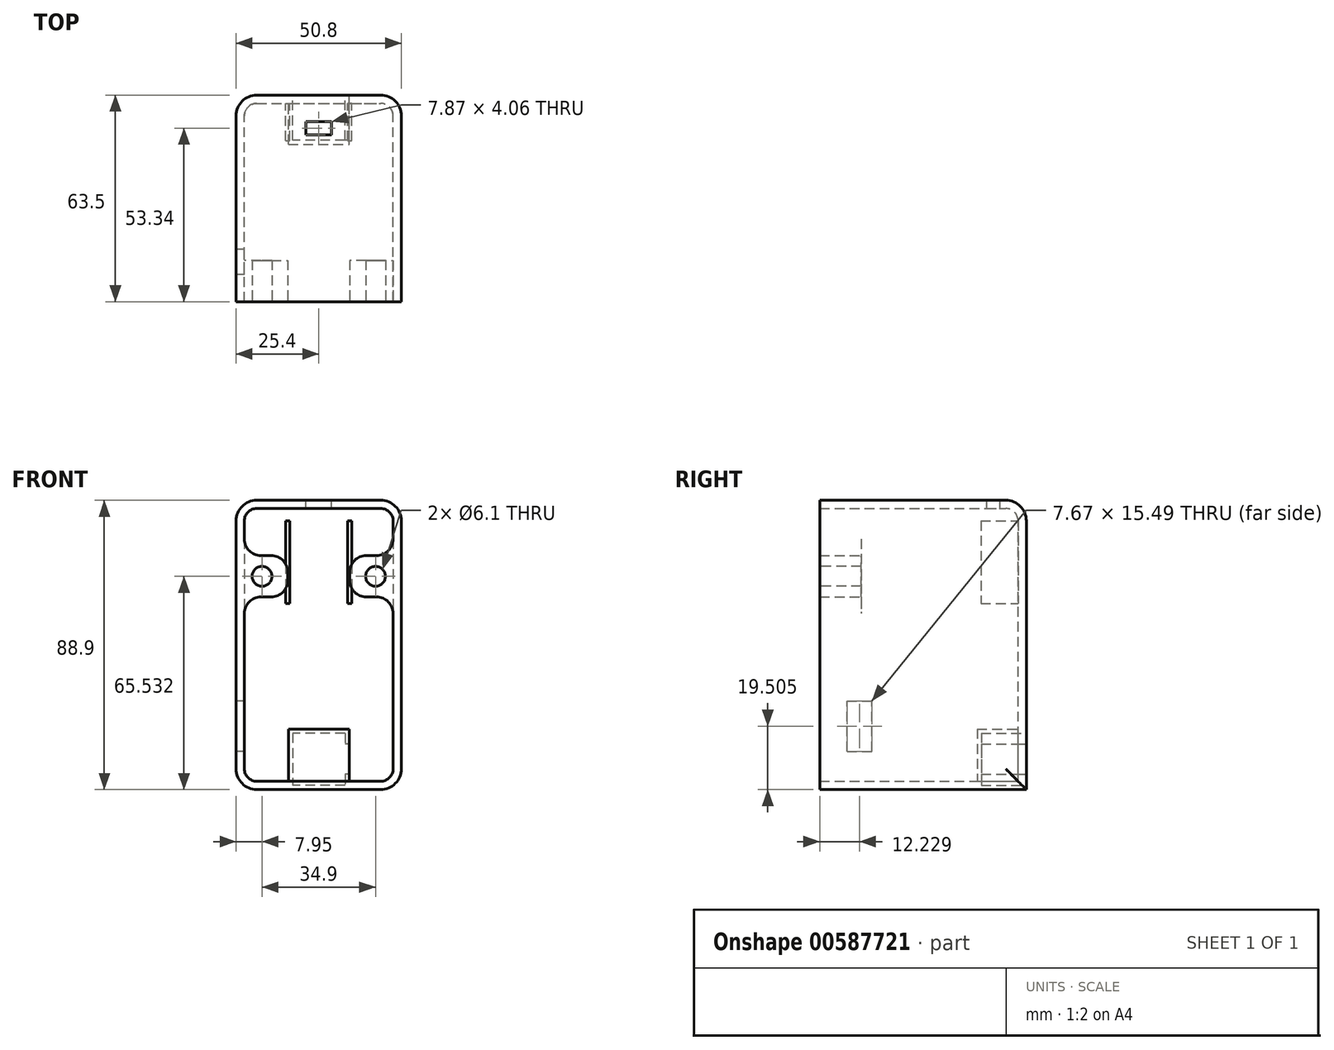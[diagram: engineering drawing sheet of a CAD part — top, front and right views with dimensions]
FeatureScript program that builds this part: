
annotation { "Feature Type Name" : "Feature", "Feature Type Description" : "" }
export const myFeature = defineFeature(function(context is Context, id is Id, definition is map)
    precondition{}
    {
        {
            var Q0;
            Q0=qCreatedBy(makeId("Front.planeOp"),FACE);
            var sketch = newSketch(context, id + "F0", { "sketchPlane" : qUnion([Q0])});
            skLineSegment(sketch, "E0.bottom", {"start": v(-25.4, 44.45) * mm, "end": v(25.4, 44.45) * mm});
            skLineSegment(sketch, "E0.top", {"start": v(-25.4, -44.45) * mm, "end": v(25.4, -44.45) * mm});
            skLineSegment(sketch, "E0.left", {"start": v(-25.4, 44.45) * mm, "end": v(-25.4, -44.45) * mm});
            skLineSegment(sketch, "E0.right", {"start": v(25.4, 44.45) * mm, "end": v(25.4, -44.45) * mm});
            skPoint(sketch, "E0.middle", {"position": v(0, 0) * mm});
            skSolve(sketch);
        }
        {
            var Q0;
            Q0 = qSketchRegion(id + "F0", true);
            extrude(context, id + "F1", {"entities" : qUnion([Q0]), "depth" : 63.5 * mm, "offsetDistance" : 25.4 * mm});
        }
        {
            var Q0;
            Q0=makeQuery(id+"F1.opExtrude","SWEPT_EDGE",EDGE,{"disambiguationData":[OSD([sQuery(id+"F0.wireOp",EDGE,"E0.bottom"),sQuery(id+"F0.wireOp",EDGE,"E0.right")])]});
            var Q1;
            Q1=makeQuery(id+"F1.opExtrude","SWEPT_EDGE",EDGE,{"disambiguationData":[OSD([sQuery(id+"F0.wireOp",EDGE,"E0.bottom"),sQuery(id+"F0.wireOp",EDGE,"E0.left")])]});
            var Q2;
            Q2=makeQuery(id+"F1.opExtrude","CAP_EDGE",EDGE,{"disambiguationData":[OSD([sQuery(id+"F0.wireOp",EDGE,"E0.bottom")])],"isStart":true});
            var Q3;
            Q3=makeQuery(id+"F1.opExtrude","SWEPT_EDGE",EDGE,{"disambiguationData":[OSD([sQuery(id+"F0.wireOp",EDGE,"E0.top"),sQuery(id+"F0.wireOp",EDGE,"E0.right")])]});
            var Q4;
            Q4=makeQuery(id+"F1.opExtrude","SWEPT_EDGE",EDGE,{"disambiguationData":[OSD([sQuery(id+"F0.wireOp",EDGE,"E0.top"),sQuery(id+"F0.wireOp",EDGE,"E0.left")])]});
            var Q5;
            Q5=makeQuery(id+"F1.opExtrude","CAP_EDGE",EDGE,{"disambiguationData":[OSD([sQuery(id+"F0.wireOp",EDGE,"E0.right")])],"isStart":true});
            var Q6;
            Q6=makeQuery(id+"F1.opExtrude","CAP_EDGE",EDGE,{"disambiguationData":[OSD([sQuery(id+"F0.wireOp",EDGE,"E0.left")])],"isStart":true});
            fillet(context, id + "F2", {"entities" : qUnion([Q0, Q1, Q2, Q3, Q4, Q5, Q6]), "radius" : 6.35 * mm, "tangentPropagation" : true, "allowEdgeOverflow" : false});
        }
        {
            var Q0;
            Q0=makeQuery(id+"F1.opExtrude","CAP_FACE",FACE,{"disambiguationData":[OSD([sQuery(id+"F0.wireOp",EDGE,"E0.bottom"),sQuery(id+"F0.wireOp",EDGE,"E0.top"),sQuery(id+"F0.wireOp",EDGE,"E0.left"),sQuery(id+"F0.wireOp",EDGE,"E0.right")])],"isStart":false});
            shell(context, id + "F3", {"entities" : qUnion([Q0]), "thickness" : 2.54 * mm});
        }
        {
            var Q0;
            Q0=makeQuery(id+"F1.opExtrude","CAP_FACE",FACE,{"disambiguationData":[OSD([sQuery(id+"F0.wireOp",EDGE,"E0.bottom"),sQuery(id+"F0.wireOp",EDGE,"E0.top"),sQuery(id+"F0.wireOp",EDGE,"E0.left"),sQuery(id+"F0.wireOp",EDGE,"E0.right")])],"isStart":false});
            var sketch = newSketch(context, id + "F4", { "sketchPlane" : qUnion([Q0])});
            skLineSegment(sketch, "E1.bottom", {"start": v(-25.4, 27.43) * mm, "end": v(-9.5, 27.43) * mm});
            skLineSegment(sketch, "E1.top", {"start": v(-25.4, 14.73) * mm, "end": v(-9.5, 14.73) * mm});
            skLineSegment(sketch, "E1.left", {"start": v(-25.4, 27.43) * mm, "end": v(-25.4, 14.73) * mm});
            skLineSegment(sketch, "E1.right", {"start": v(-9.5, 27.43) * mm, "end": v(-9.5, 14.73) * mm});
            skCircle(sketch, "E2", {"center": v(-17.45, 21.08) * mm, "radius": 3.05 * mm});
            skPoint(sketch, "E2.centerSnap0", {"position": v(-9.5, 21.08) * mm});
            skPoint(sketch, "E2.centerSnap1", {"position": v(-17.45, 27.43) * mm});
            skLineSegment(sketch, "E3", {"start": v(0, 84.41) * mm, "end": v(0, -83.5) * mm, "construction": true});
            skLineSegment(sketch, "E4.MirrorCS", {"start": v(25.4, 27.43) * mm, "end": v(9.5, 27.43) * mm});
            skLineSegment(sketch, "E5.MirrorCS", {"start": v(9.5, 27.43) * mm, "end": v(9.5, 14.73) * mm});
            skLineSegment(sketch, "E6.MirrorCS", {"start": v(25.4, 14.73) * mm, "end": v(9.5, 14.73) * mm});
            skCircle(sketch, "E7.MirrorC", {"center": v(17.45, 21.08) * mm, "radius": 3.05 * mm});
            skLineSegment(sketch, "E8", {"start": v(25.4, 27.43) * mm, "end": v(25.4, 14.73) * mm});
            skSolve(sketch);
        }
        {
            var Q0;
            Q0 = qSketchRegion(id + "F4", true);
            extrude(context, id + "F5", {"entities" : qUnion([Q0]), "operationType" : NewBodyOperationType.ADD, "oppositeDirection" : true, "depth" : 12.7 * mm, "offsetDistance" : 25.4 * mm});
        }
        {
            var Q0;
            Q0=makeQuery(id+"F5.opExtrude","SWEPT_EDGE",EDGE,{"disambiguationData":[OSD([sQuery(id+"F4.wireOp",EDGE,"E1.bottom"),sQuery(id+"F4.wireOp",EDGE,"E1.right")])]});
            var Q1;
            Q1=makeQuery(id+"F5.opExtrude","SWEPT_EDGE",EDGE,{"disambiguationData":[OSD([sQuery(id+"F4.wireOp",EDGE,"E1.top"),sQuery(id+"F4.wireOp",EDGE,"E1.right")])]});
            var Q2;
            Q2=makeQuery(id+"F5.opExtrude","SWEPT_EDGE",EDGE,{"disambiguationData":[OSD([sQuery(id+"F4.wireOp",EDGE,"E5.MirrorCS"),sQuery(id+"F4.wireOp",EDGE,"E6.MirrorCS")])]});
            var Q3;
            Q3=makeQuery(id+"F5.opExtrude","SWEPT_EDGE",EDGE,{"disambiguationData":[OSD([sQuery(id+"F4.wireOp",EDGE,"E4.MirrorCS"),sQuery(id+"F4.wireOp",EDGE,"E5.MirrorCS")])]});
            var Q4;
            {var subQ0=sQuery(id+"F0.wireOp",EDGE,"E0.left");Q4=makeQuery(id+"F5.boolean.opBoolean","INTERSECT",EDGE,{"derivedFrom":[makeQuery(id+"F3.opShell","OFFSET_FACE",FACE,{"disambiguationData":[OSD([subQ0]),TDD([makeQuery(id+"F1.opExtrude","SWEPT_FACE",FACE,{"disambiguationData":[OSD([subQ0])]})])]}),makeQuery(id+"F5.opExtrude","SWEPT_FACE",FACE,{"disambiguationData":[OSD([sQuery(id+"F4.wireOp",EDGE,"E1.bottom")])]})]});}
            var Q5;
            {var subQ0=sQuery(id+"F0.wireOp",EDGE,"E0.right");Q5=makeQuery(id+"F5.boolean.opBoolean","INTERSECT",EDGE,{"derivedFrom":[makeQuery(id+"F3.opShell","OFFSET_FACE",FACE,{"disambiguationData":[OSD([subQ0]),TDD([makeQuery(id+"F1.opExtrude","SWEPT_FACE",FACE,{"disambiguationData":[OSD([subQ0])]})])]}),makeQuery(id+"F5.opExtrude","SWEPT_FACE",FACE,{"disambiguationData":[OSD([sQuery(id+"F4.wireOp",EDGE,"E4.MirrorCS")])]})]});}
            var Q6;
            {var subQ0=sQuery(id+"F0.wireOp",EDGE,"E0.left");Q6=makeQuery(id+"F5.boolean.opBoolean","INTERSECT",EDGE,{"derivedFrom":[makeQuery(id+"F3.opShell","OFFSET_FACE",FACE,{"disambiguationData":[OSD([subQ0]),TDD([makeQuery(id+"F1.opExtrude","SWEPT_FACE",FACE,{"disambiguationData":[OSD([subQ0])]})])]}),makeQuery(id+"F5.opExtrude","SWEPT_FACE",FACE,{"disambiguationData":[OSD([sQuery(id+"F4.wireOp",EDGE,"E1.top")])]})]});}
            var Q7;
            {var subQ0=sQuery(id+"F0.wireOp",EDGE,"E0.right");Q7=makeQuery(id+"F5.boolean.opBoolean","INTERSECT",EDGE,{"derivedFrom":[makeQuery(id+"F3.opShell","OFFSET_FACE",FACE,{"disambiguationData":[OSD([subQ0]),TDD([makeQuery(id+"F1.opExtrude","SWEPT_FACE",FACE,{"disambiguationData":[OSD([subQ0])]})])]}),makeQuery(id+"F5.opExtrude","SWEPT_FACE",FACE,{"disambiguationData":[OSD([sQuery(id+"F4.wireOp",EDGE,"E6.MirrorCS")])]})]});}
            fillet(context, id + "F6", {"entities" : qUnion([Q0, Q1, Q2, Q3, Q4, Q5, Q6, Q7]), "radius" : 5.08 * mm, "tangentPropagation" : true, "allowEdgeOverflow" : false});
        }
        {
            var Q0;
            Q0=makeQuery(id+"F1.opExtrude","SWEPT_FACE",FACE,{"disambiguationData":[OSD([sQuery(id+"F0.wireOp",EDGE,"E0.bottom")])]});
            var sketch = newSketch(context, id + "F7", { "sketchPlane" : qUnion([Q0])});
            skLineSegment(sketch, "E9.bottom", {"start": v(3.94, -12.2) * mm, "end": v(-3.94, -12.2) * mm});
            skLineSegment(sketch, "E9.top", {"start": v(3.94, -8.13) * mm, "end": v(-3.94, -8.13) * mm});
            skLineSegment(sketch, "E9.left", {"start": v(3.94, -12.2) * mm, "end": v(3.94, -8.13) * mm});
            skLineSegment(sketch, "E9.right", {"start": v(-3.94, -12.2) * mm, "end": v(-3.94, -8.13) * mm});
            skPoint(sketch, "E9.middle", {"position": v(0, -10.16) * mm});
            skSolve(sketch);
        }
        {
            var Q0;
            Q0 = qSketchRegion(id + "F7", true);
            extrude(context, id + "F8", {"entities" : qUnion([Q0]), "operationType" : NewBodyOperationType.REMOVE, "oppositeDirection" : true, "depth" : 25.4 * mm, "offsetDistance" : 25.4 * mm});
        }
        {
            var Q0;
            Q0=makeQuery(id+"F3.opShell","OFFSET_FACE",FACE,{"disambiguationData":[OSD([sQuery(id+"F0.wireOp",EDGE,"E0.bottom"),sQuery(id+"F0.wireOp",EDGE,"E0.top"),sQuery(id+"F0.wireOp",EDGE,"E0.left"),sQuery(id+"F0.wireOp",EDGE,"E0.right")])]});
            var sketch = newSketch(context, id + "F9", { "sketchPlane" : qUnion([Q0])});
            skLineSegment(sketch, "E10.bottom", {"start": v(-10.16, 38.1) * mm, "end": v(-8.9, 38.1) * mm});
            skLineSegment(sketch, "E10.top", {"start": v(-10.16, 12.7) * mm, "end": v(-8.9, 12.7) * mm});
            skLineSegment(sketch, "E10.left", {"start": v(-10.16, 38.1) * mm, "end": v(-10.16, 12.7) * mm});
            skLineSegment(sketch, "E10.right", {"start": v(-8.9, 38.1) * mm, "end": v(-8.9, 12.7) * mm});
            skLineSegment(sketch, "E11", {"start": v(0, 0) * mm, "end": v(0, 27.98) * mm, "construction": true});
            skLineSegment(sketch, "E12.MirrorCS", {"start": v(10.16, 38.1) * mm, "end": v(8.9, 38.1) * mm});
            skLineSegment(sketch, "E13.MirrorCS", {"start": v(10.16, 12.7) * mm, "end": v(8.9, 12.7) * mm});
            skLineSegment(sketch, "E14.MirrorCS", {"start": v(10.16, 38.1) * mm, "end": v(10.16, 12.7) * mm});
            skLineSegment(sketch, "E15.MirrorCS", {"start": v(8.9, 38.1) * mm, "end": v(8.9, 12.7) * mm});
            skSolve(sketch);
        }
        {
            var Q0;
            Q0 = qSketchRegion(id + "F9", true);
            extrude(context, id + "F10", {"entities" : qUnion([Q0]), "operationType" : NewBodyOperationType.ADD, "depth" : 11.43 * mm, "offsetDistance" : 25.4 * mm});
        }
        {
            var Q0;
            Q0=makeQuery(id+"F1.opExtrude","CAP_FACE",FACE,{"disambiguationData":[OSD([sQuery(id+"F0.wireOp",EDGE,"E0.bottom"),sQuery(id+"F0.wireOp",EDGE,"E0.top"),sQuery(id+"F0.wireOp",EDGE,"E0.left"),sQuery(id+"F0.wireOp",EDGE,"E0.right")])],"isStart":true});
            var sketch = newSketch(context, id + "F11", { "sketchPlane" : qUnion([Q0])});
            skLineSegment(sketch, "E16.bottom", {"start": v(-8.06, -27.13) * mm, "end": v(8.06, -27.13) * mm});
            skLineSegment(sketch, "E16.top", {"start": v(-8.06, -43.18) * mm, "end": v(8.06, -43.18) * mm});
            skLineSegment(sketch, "E16.left", {"start": v(-8.06, -27.13) * mm, "end": v(-8.06, -43.18) * mm});
            skLineSegment(sketch, "E16.right", {"start": v(8.06, -27.13) * mm, "end": v(8.06, -43.18) * mm});
            skPoint(sketch, "E17", {"position": v(0, -27.13) * mm});
            skLineSegment(sketch, "E18.bottom", {"start": v(-9.33, -25.86) * mm, "end": v(9.33, -25.86) * mm});
            skLineSegment(sketch, "E18.top", {"start": v(-9.33, -44.45) * mm, "end": v(9.33, -44.45) * mm});
            skLineSegment(sketch, "E18.left", {"start": v(-9.33, -25.86) * mm, "end": v(-9.33, -44.45) * mm});
            skLineSegment(sketch, "E18.right", {"start": v(9.33, -25.86) * mm, "end": v(9.33, -44.45) * mm});
            skSolve(sketch);
        }
        {
            var Q0;
            {var subQ0=sQuery(id+"F11.wireOp",EDGE,"E16.bottom");Q0=makeQuery(id+"F11.imprint","IMPRINT",FACE,{"disambiguationData":[TD([[makeQuery(id+"F11.imprint","IMPRINT",EDGE,{"derivedFrom":subQ0}),-1.0]])]});}
            var Q1;
            {var subQ0=sQuery(id+"F11.wireOp",EDGE,"E16.top");Q1=makeQuery(id+"F11.imprint","IMPRINT",FACE,{"disambiguationData":[TD([[makeQuery(id+"F11.imprint","IMPRINT",EDGE,{"derivedFrom":subQ0}),1.0]])]});}
            extrude(context, id + "F12", {"entities" : qUnion([Q0, Q1]), "operationType" : NewBodyOperationType.REMOVE, "oppositeDirection" : true, "depth" : 13.84 * mm, "offsetDistance" : 25.4 * mm});
        }
        {
            var Q0;
            Q0=makeQuery(id+"F11.imprint","IMPRINT",FACE,{"disambiguationData":[TD([[makeQuery(id+"F11.imprint","IMPRINT",EDGE,{"derivedFrom":sQuery(id+"F11.wireOp",EDGE,"E16.bottom")}),1.0]])]});
            extrude(context, id + "F13", {"entities" : qUnion([Q0]), "operationType" : NewBodyOperationType.ADD, "oppositeDirection" : true, "depth" : 13.84 * mm, "offsetDistance" : 25.4 * mm});
        }
        {
            var Q0;
            Q0=makeQuery(id+"F11.imprint","IMPRINT",FACE,{"disambiguationData":[TD([[makeQuery(id+"F11.imprint","IMPRINT",EDGE,{"derivedFrom":sQuery(id+"F11.wireOp",EDGE,"E18.bottom")}),1.0]])]});
            var sketch = newSketch(context, id + "F14", { "sketchPlane" : qUnion([Q0])});
            skLineSegment(sketch, "E19.bottom", {"start": v(-9.33, -30.52) * mm, "end": v(-5.57, -30.52) * mm});
            skLineSegment(sketch, "E19.top", {"start": v(-9.33, -39.79) * mm, "end": v(-5.57, -39.79) * mm});
            skLineSegment(sketch, "E19.left", {"start": v(-9.33, -30.52) * mm, "end": v(-9.33, -39.79) * mm});
            skLineSegment(sketch, "E19.right", {"start": v(-5.57, -30.52) * mm, "end": v(-5.57, -39.79) * mm});
            skPoint(sketch, "E19.middle", {"position": v(-7.45, -35.15) * mm});
            skPoint(sketch, "E20", {"position": v(-9.33, -35.15) * mm});
            skSolve(sketch);
        }
        {
            var Q0;
            Q0 = qSketchRegion(id + "F14", true);
            extrude(context, id + "F15", {"entities" : qUnion([Q0]), "operationType" : NewBodyOperationType.REMOVE, "oppositeDirection" : true, "depth" : 13.84 * mm, "offsetDistance" : 25.4 * mm});
        }
        {
            var Q0;
            {var subQ0=sQuery(id+"F11.wireOp",EDGE,"E18.bottom");var subQ1=sQuery(id+"F11.wireOp",EDGE,"E16.left");var subQ2=sQuery(id+"F11.wireOp",EDGE,"E16.bottom");var subQ3=sQuery(id+"F11.wireOp",EDGE,"E16.right");var subQ4=sQuery(id+"F11.wireOp",EDGE,"E18.left");var subQ5=sQuery(id+"F11.wireOp",EDGE,"E16.top");var subQ6=sQuery(id+"F11.wireOp",EDGE,"E18.right");Q0=makeQuery(id+"F15.boolean.opBoolean","SPLIT",FACE,{"disambiguationData":[TD([makeQuery(id+"F12.boolean.opBoolean","COPY",FACE,{"derivedFrom":makeQuery(id+"F12.opExtrude","SWEPT_FACE",FACE,{"disambiguationData":[OSD([subQ2])]})})])],"derivedFrom":makeQuery(id+"F13.opExtrude","CAP_FACE",FACE,{"disambiguationData":[OSD([subQ2,subQ5,subQ1,subQ3,subQ0,sQuery(id+"F11.wireOp",EDGE,"E18.top"),subQ4,subQ6])],"isStart":false})});}
            var sketch = newSketch(context, id + "F16", { "sketchPlane" : qUnion([Q0])});
            skLineSegment(sketch, "E21.bottom", {"start": v(-9.33, -25.86) * mm, "end": v(9.33, -25.86) * mm});
            skLineSegment(sketch, "E21.top", {"start": v(-9.33, -44.45) * mm, "end": v(9.33, -44.45) * mm});
            skLineSegment(sketch, "E21.left", {"start": v(-9.33, -25.86) * mm, "end": v(-9.33, -44.45) * mm});
            skLineSegment(sketch, "E21.right", {"start": v(9.33, -25.86) * mm, "end": v(9.33, -44.45) * mm});
            skSolve(sketch);
        }
        {
            var Q0;
            Q0 = qSketchRegion(id + "F16", true);
            extrude(context, id + "F17", {"entities" : qUnion([Q0]), "operationType" : NewBodyOperationType.ADD, "depth" : 1.27 * mm, "offsetDistance" : 25.4 * mm});
        }
        {
            var Q0;
            Q0=makeQuery(id+"F1.opExtrude","SWEPT_FACE",FACE,{"disambiguationData":[OSD([sQuery(id+"F0.wireOp",EDGE,"E0.left")])]});
            var sketch = newSketch(context, id + "F18", { "sketchPlane" : qUnion([Q0])});
            skLineSegment(sketch, "E22.bottom", {"start": v(47.44, -17.2) * mm, "end": v(55.1, -17.2) * mm});
            skLineSegment(sketch, "E22.top", {"start": v(47.44, -32.7) * mm, "end": v(55.1, -32.7) * mm});
            skLineSegment(sketch, "E22.left", {"start": v(47.44, -17.2) * mm, "end": v(47.44, -32.7) * mm});
            skLineSegment(sketch, "E22.right", {"start": v(55.1, -17.2) * mm, "end": v(55.1, -32.7) * mm});
            skSolve(sketch);
        }
        {
            var Q0;
            Q0 = qSketchRegion(id + "F18", true);
            extrude(context, id + "F19", {"entities" : qUnion([Q0]), "operationType" : NewBodyOperationType.REMOVE, "oppositeDirection" : true, "depth" : 25.4 * mm, "offsetDistance" : 25.4 * mm});
        }
    });
